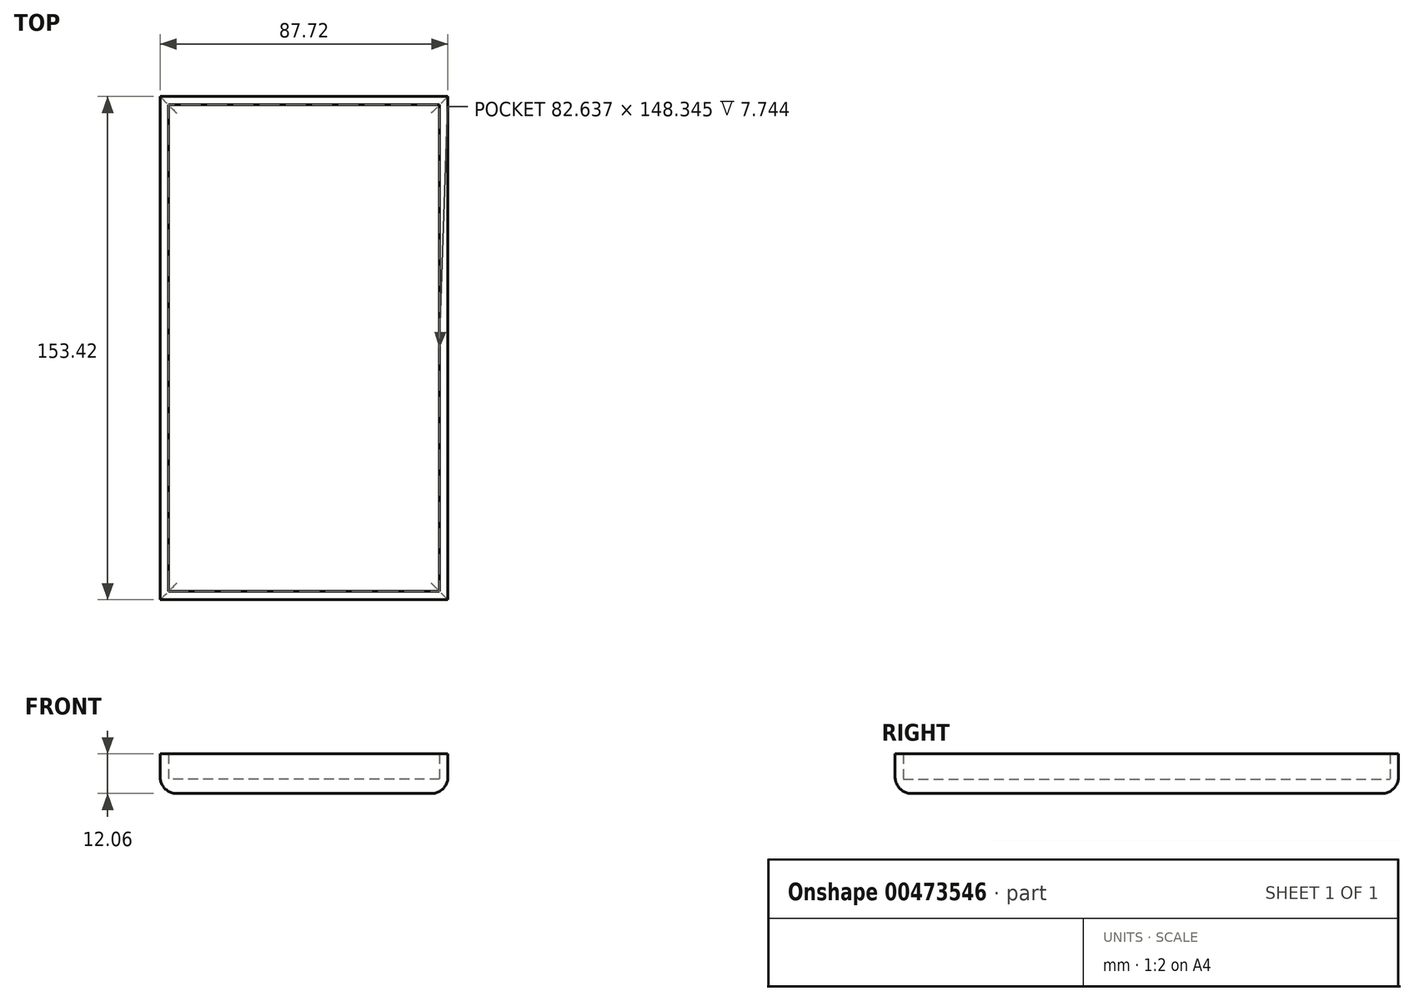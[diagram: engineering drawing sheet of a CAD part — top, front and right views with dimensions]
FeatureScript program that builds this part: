
annotation { "Feature Type Name" : "Feature", "Feature Type Description" : "" }
export const myFeature = defineFeature(function(context is Context, id is Id, definition is map)
    precondition{}
    {
        {
            var Q0;
            Q0=qCreatedBy(makeId("Top.planeOp"),FACE);
            var sketch = newSketch(context, id + "F0", { "sketchPlane" : qUnion([Q0])});
            skLineSegment(sketch, "E0.bottom", {"start": v(43.86, -76.71) * mm, "end": v(-43.86, -76.71) * mm});
            skLineSegment(sketch, "E0.top", {"start": v(43.86, 76.71) * mm, "end": v(-43.86, 76.71) * mm});
            skLineSegment(sketch, "E0.left", {"start": v(43.86, -76.71) * mm, "end": v(43.86, 76.71) * mm});
            skLineSegment(sketch, "E0.right", {"start": v(-43.86, -76.71) * mm, "end": v(-43.86, 76.71) * mm});
            skPoint(sketch, "E0.middle", {"position": v(0, 0) * mm});
            skSolve(sketch);
        }
        {
            var Q0;
            Q0=makeQuery(id+"F0.imprint","IMPRINT",FACE,{"disambiguationData":[TD([[makeQuery(id+"F0.imprint","IMPRINT",EDGE,{"derivedFrom":sQuery(id+"F0.wireOp",EDGE,"E0.bottom")}),-1.0]])]});
            extrude(context, id + "F1", {"entities" : qUnion([Q0]), "depth" : 1.77 * mm});
        }
        {
            var Q0;
            Q0=makeQuery(id+"F1.opExtrude","CAP_FACE",FACE,{"disambiguationData":[OSD([sQuery(id+"F0.wireOp",EDGE,"E0.bottom"),sQuery(id+"F0.wireOp",EDGE,"E0.top"),sQuery(id+"F0.wireOp",EDGE,"E0.left"),sQuery(id+"F0.wireOp",EDGE,"E0.right")])],"isStart":false});
            var sketch = newSketch(context, id + "F2", { "sketchPlane" : qUnion([Q0])});
            skSolve(sketch);
        }
        {
            var Q0;
            Q0=makeQuery(id+"F2.imprint","IMPRINT",FACE,{"disambiguationData":[TD([[makeQuery(id+"F2.imprint","IMPRINT",EDGE,{"derivedFrom":makeQuery(id+"F1.opExtrude","CAP_EDGE",EDGE,{"disambiguationData":[OSD([sQuery(id+"F0.wireOp",EDGE,"E0.bottom")])],"isStart":false})}),-1.0]])]});
            extrude(context, id + "F3", {"entities" : qUnion([Q0]), "operationType" : NewBodyOperationType.ADD, "depth" : 5.97 * mm});
        }
        {
            var Q0;
            Q0=makeQuery(id+"F3.opExtrude","CAP_FACE",FACE,{"disambiguationData":[OSD([sQuery(id+"F0.wireOp",EDGE,"E0.bottom"),sQuery(id+"F0.wireOp",EDGE,"E0.top"),sQuery(id+"F0.wireOp",EDGE,"E0.left"),sQuery(id+"F0.wireOp",EDGE,"E0.right")])],"isStart":false});
            shell(context, id + "F4", {"entities" : qUnion([Q0]), "thickness" : 2.54 * mm});
        }
        {
            var Q0;
            Q0=makeQuery(id+"F3.opExtrude","CAP_FACE",FACE,{"disambiguationData":[OSD([sQuery(id+"F0.wireOp",EDGE,"E0.bottom"),sQuery(id+"F0.wireOp",EDGE,"E0.top"),sQuery(id+"F0.wireOp",EDGE,"E0.left"),sQuery(id+"F0.wireOp",EDGE,"E0.right")])],"isStart":false});
            var Q1;
            Q1=makeQuery(id+"F1.opExtrude","CAP_FACE",FACE,{"disambiguationData":[OSD([sQuery(id+"F0.wireOp",EDGE,"E0.bottom"),sQuery(id+"F0.wireOp",EDGE,"E0.top"),sQuery(id+"F0.wireOp",EDGE,"E0.left"),sQuery(id+"F0.wireOp",EDGE,"E0.right")])],"isStart":true});
            extrude(context, id + "F5", {"entities" : qUnion([Q0, Q1]), "operationType" : NewBodyOperationType.ADD, "depth" : 4.32 * mm});
        }
        {
            var Q0;
            Q0=makeQuery(id+"F1.opExtrude","CAP_FACE",FACE,{"disambiguationData":[OSD([sQuery(id+"F0.wireOp",EDGE,"E0.bottom"),sQuery(id+"F0.wireOp",EDGE,"E0.top"),sQuery(id+"F0.wireOp",EDGE,"E0.left"),sQuery(id+"F0.wireOp",EDGE,"E0.right")])],"isStart":true});
            fillet(context, id + "F6", {"entities" : qUnion([Q0]), "radius" : 5.08 * mm, "tangentPropagation" : true, "allowEdgeOverflow" : false});
        }
    });
